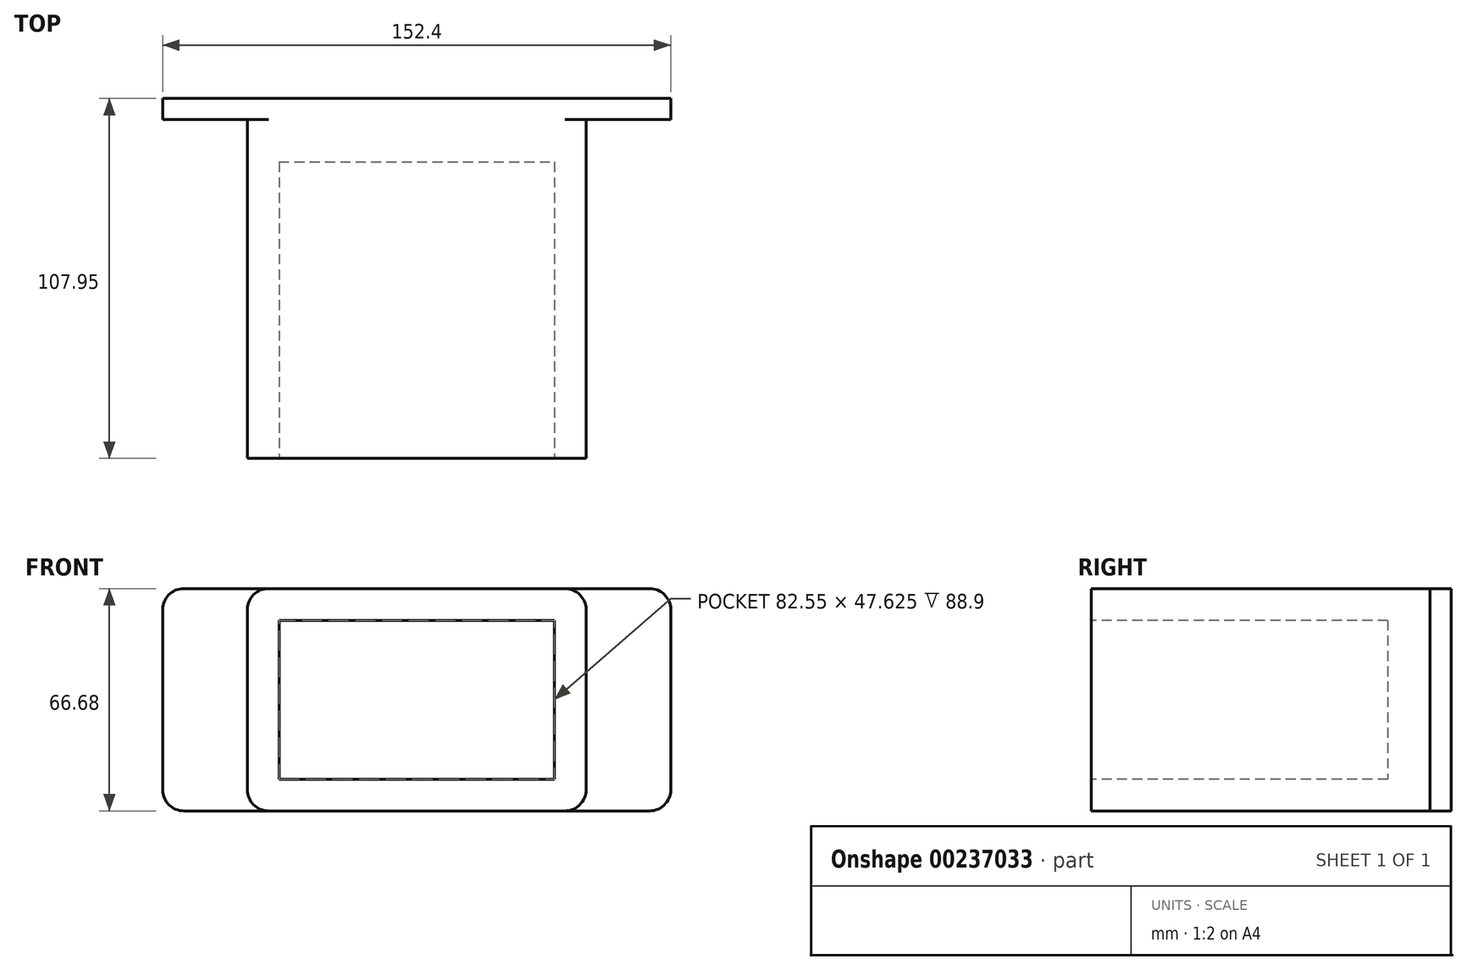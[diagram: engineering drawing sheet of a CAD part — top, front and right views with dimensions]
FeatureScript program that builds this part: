
annotation { "Feature Type Name" : "Feature", "Feature Type Description" : "" }
export const myFeature = defineFeature(function(context is Context, id is Id, definition is map)
    precondition{}
    {
        {
            var Q0;
            Q0=qCreatedBy(makeId("Front.planeOp"),FACE);
            var sketch = newSketch(context, id + "F0", { "sketchPlane" : qUnion([Q0])});
            skLineSegment(sketch, "E0.bottom", {"start": v(76.2, -33.34) * mm, "end": v(-76.2, -33.34) * mm});
            skLineSegment(sketch, "E0.top", {"start": v(76.2, 33.34) * mm, "end": v(-76.2, 33.34) * mm});
            skLineSegment(sketch, "E0.left", {"start": v(76.2, -33.34) * mm, "end": v(76.2, 33.34) * mm});
            skLineSegment(sketch, "E0.right", {"start": v(-76.2, -33.34) * mm, "end": v(-76.2, 33.34) * mm});
            skPoint(sketch, "E0.middle", {"position": v(0, 0) * mm});
            skSolve(sketch);
        }
        {
            var Q0;
            Q0=makeQuery(id+"F0.imprint","IMPRINT",FACE,{"disambiguationData":[TD([[makeQuery(id+"F0.imprint","IMPRINT",EDGE,{"derivedFrom":sQuery(id+"F0.wireOp",EDGE,"E0.bottom")}),-1.0]])]});
            extrude(context, id + "F1", {"entities" : qUnion([Q0]), "depth" : 6.35 * mm});
        }
        {
            var Q0;
            Q0=makeQuery(id+"F1.opExtrude","CAP_FACE",FACE,{"disambiguationData":[OSD([sQuery(id+"F0.wireOp",EDGE,"E0.bottom"),sQuery(id+"F0.wireOp",EDGE,"E0.top"),sQuery(id+"F0.wireOp",EDGE,"E0.left"),sQuery(id+"F0.wireOp",EDGE,"E0.right")])],"isStart":false});
            var sketch = newSketch(context, id + "F2", { "sketchPlane" : qUnion([Q0])});
            skLineSegment(sketch, "E1.bottom", {"start": v(50.8, 33.34) * mm, "end": v(-50.8, 33.34) * mm});
            skLineSegment(sketch, "E1.top", {"start": v(50.8, -33.34) * mm, "end": v(-50.8, -33.34) * mm});
            skLineSegment(sketch, "E1.left", {"start": v(50.8, 33.34) * mm, "end": v(50.8, -33.34) * mm});
            skLineSegment(sketch, "E1.right", {"start": v(-50.8, 33.34) * mm, "end": v(-50.8, -33.34) * mm});
            skPoint(sketch, "E1.middle", {"position": v(0, 0) * mm});
            skSolve(sketch);
        }
        {
            var Q0;
            Q0 = qSketchRegion(id + "F2", true);
            extrude(context, id + "F3", {"entities" : qUnion([Q0]), "operationType" : NewBodyOperationType.ADD, "depth" : 101.6 * mm});
        }
        {
            var Q0;
            Q0=makeQuery(id+"F3.opExtrude","SWEPT_EDGE",EDGE,{"disambiguationData":[OSD([sQuery(id+"F0.wireOp",EDGE,"E0.top"),sQuery(id+"F2.wireOp",EDGE,"E1.bottom"),sQuery(id+"F2.wireOp",EDGE,"E1.right")])]});
            var Q1;
            Q1=makeQuery(id+"F1.opExtrude","SWEPT_EDGE",EDGE,{"disambiguationData":[OSD([sQuery(id+"F0.wireOp",EDGE,"E0.top"),sQuery(id+"F0.wireOp",EDGE,"E0.right")])]});
            var Q2;
            Q2=makeQuery(id+"F1.opExtrude","SWEPT_EDGE",EDGE,{"disambiguationData":[OSD([sQuery(id+"F0.wireOp",EDGE,"E0.bottom"),sQuery(id+"F0.wireOp",EDGE,"E0.right")])]});
            var Q3;
            Q3=makeQuery(id+"F3.opExtrude","SWEPT_EDGE",EDGE,{"disambiguationData":[OSD([sQuery(id+"F0.wireOp",EDGE,"E0.bottom"),sQuery(id+"F2.wireOp",EDGE,"E1.top"),sQuery(id+"F2.wireOp",EDGE,"E1.left")])]});
            var Q4;
            Q4=makeQuery(id+"F3.opExtrude","SWEPT_EDGE",EDGE,{"disambiguationData":[OSD([sQuery(id+"F0.wireOp",EDGE,"E0.bottom"),sQuery(id+"F2.wireOp",EDGE,"E1.top"),sQuery(id+"F2.wireOp",EDGE,"E1.right")])]});
            var Q5;
            Q5=makeQuery(id+"F3.opExtrude","SWEPT_EDGE",EDGE,{"disambiguationData":[OSD([sQuery(id+"F0.wireOp",EDGE,"E0.top"),sQuery(id+"F2.wireOp",EDGE,"E1.bottom"),sQuery(id+"F2.wireOp",EDGE,"E1.left")])]});
            var Q6;
            Q6=makeQuery(id+"F1.opExtrude","SWEPT_EDGE",EDGE,{"disambiguationData":[OSD([sQuery(id+"F0.wireOp",EDGE,"E0.top"),sQuery(id+"F0.wireOp",EDGE,"E0.left")])]});
            var Q7;
            Q7=makeQuery(id+"F1.opExtrude","SWEPT_EDGE",EDGE,{"disambiguationData":[OSD([sQuery(id+"F0.wireOp",EDGE,"E0.bottom"),sQuery(id+"F0.wireOp",EDGE,"E0.left")])]});
            fillet(context, id + "F4", {"entities" : qUnion([Q0, Q1, Q2, Q3, Q4, Q5, Q6, Q7]), "radius" : 6.35 * mm, "tangentPropagation" : true, "allowEdgeOverflow" : false});
        }
        {
            var Q0;
            Q0=makeQuery(id+"F3.opExtrude","CAP_FACE",FACE,{"disambiguationData":[OSD([sQuery(id+"F2.wireOp",EDGE,"E1.bottom"),sQuery(id+"F2.wireOp",EDGE,"E1.top"),sQuery(id+"F2.wireOp",EDGE,"E1.left"),sQuery(id+"F2.wireOp",EDGE,"E1.right")])],"isStart":false});
            var sketch = newSketch(context, id + "F5", { "sketchPlane" : qUnion([Q0])});
            skLineSegment(sketch, "E2.bottom", {"start": v(-41.28, 23.81) * mm, "end": v(41.28, 23.81) * mm});
            skLineSegment(sketch, "E2.top", {"start": v(-41.28, -23.81) * mm, "end": v(41.28, -23.81) * mm});
            skLineSegment(sketch, "E2.left", {"start": v(-41.28, 23.81) * mm, "end": v(-41.28, -23.81) * mm});
            skLineSegment(sketch, "E2.right", {"start": v(41.28, 23.81) * mm, "end": v(41.28, -23.81) * mm});
            skPoint(sketch, "E2.middle", {"position": v(0, 0) * mm});
            skSolve(sketch);
        }
        {
            var Q0;
            Q0 = qSketchRegion(id + "F5", true);
            extrude(context, id + "F6", {"entities" : qUnion([Q0]), "operationType" : NewBodyOperationType.REMOVE, "oppositeDirection" : true, "depth" : 88.9 * mm});
        }
    });
